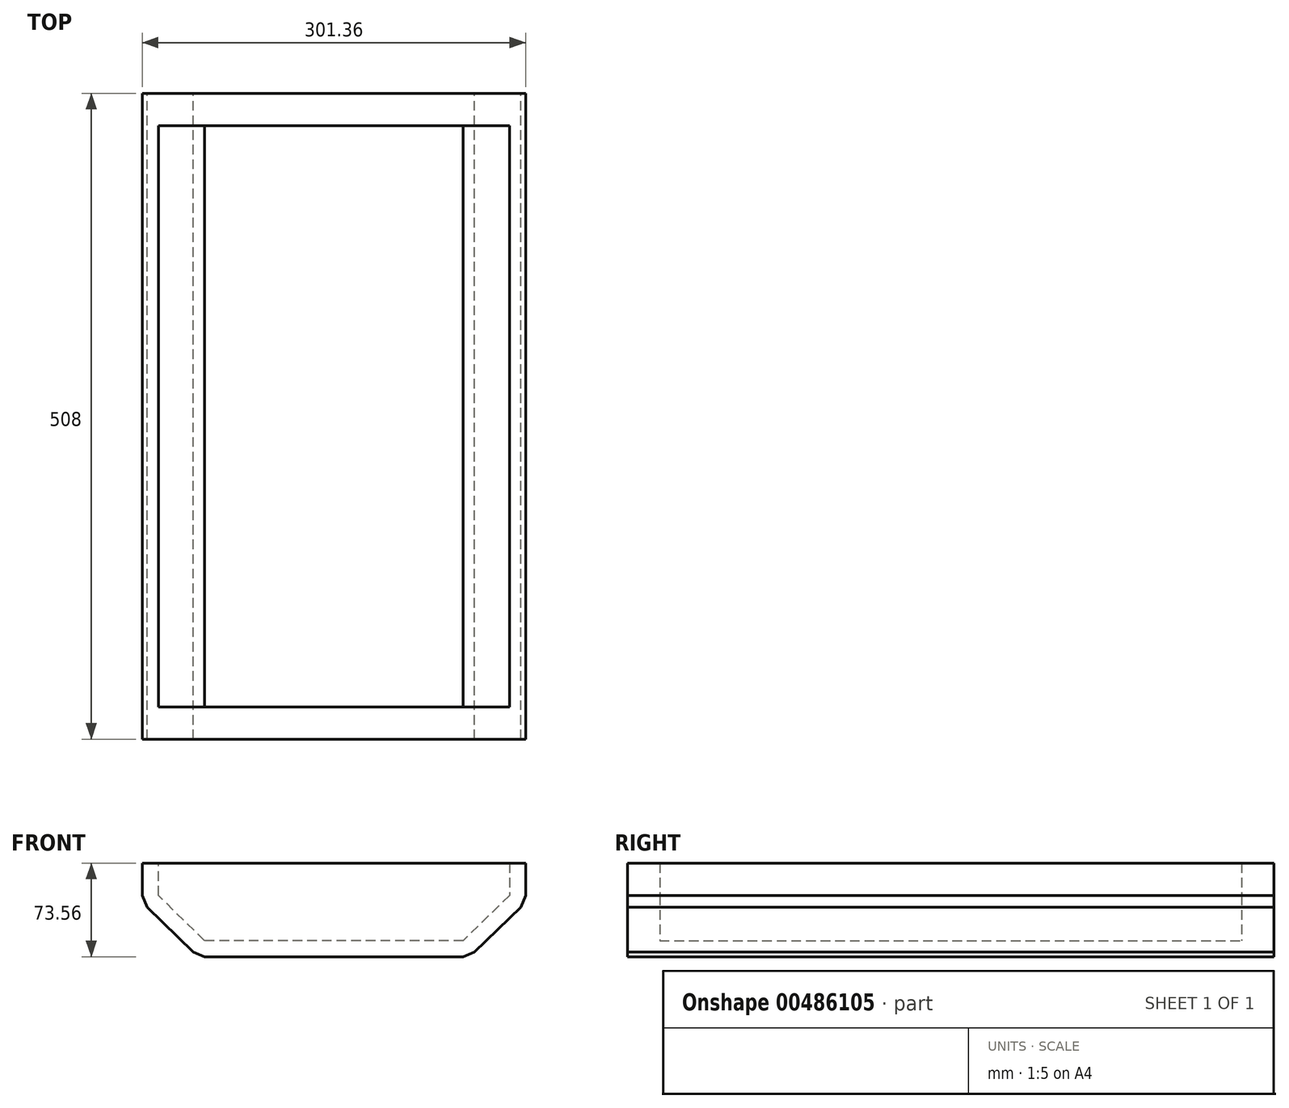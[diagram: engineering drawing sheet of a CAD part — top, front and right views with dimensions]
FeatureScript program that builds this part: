
annotation { "Feature Type Name" : "Feature", "Feature Type Description" : "" }
export const myFeature = defineFeature(function(context is Context, id is Id, definition is map)
    precondition{}
    {
        {
            var Q0;
            Q0=qCreatedBy(makeId("Front.planeOp"),FACE);
            var sketch = newSketch(context, id + "F0", { "sketchPlane" : qUnion([Q0])});
            skLineSegment(sketch, "E0", {"start": v(96.03, 17.25) * mm, "end": v(96.03, -8.15) * mm});
            skLineSegment(sketch, "E1", {"start": v(96.03, -8.15) * mm, "end": v(59.65, -43.61) * mm});
            skLineSegment(sketch, "E2", {"start": v(59.65, -43.61) * mm, "end": v(-143.55, -43.61) * mm});
            skLineSegment(sketch, "E3", {"start": v(-143.55, -43.61) * mm, "end": v(-179.93, -8.15) * mm});
            skLineSegment(sketch, "E4", {"start": v(-179.93, -8.15) * mm, "end": v(-179.93, 17.25) * mm});
            skLineSegment(sketch, "E5", {"start": v(-179.93, -8.15) * mm, "end": v(-188.8, -17.25) * mm});
            skLineSegment(sketch, "E6", {"start": v(96.03, -8.15) * mm, "end": v(104.9, -17.25) * mm});
            skLineSegment(sketch, "E7", {"start": v(-179.93, 17.25) * mm, "end": v(-192.63, 17.25) * mm});
            skLineSegment(sketch, "E8", {"start": v(96.03, 17.25) * mm, "end": v(108.73, 17.25) * mm});
            skLineSegment(sketch, "E9", {"start": v(59.65, -43.61) * mm, "end": v(68.52, -52.7) * mm});
            skLineSegment(sketch, "E10", {"start": v(-143.55, -43.61) * mm, "end": v(-152.41, -52.7) * mm});
            skLineSegment(sketch, "E11", {"start": v(-188.8, -17.25) * mm, "end": v(-152.41, -52.7) * mm});
            skLineSegment(sketch, "E12", {"start": v(-143.55, -43.61) * mm, "end": v(-143.55, -56.31) * mm});
            skLineSegment(sketch, "E13", {"start": v(59.65, -43.61) * mm, "end": v(59.65, -56.31) * mm});
            skLineSegment(sketch, "E14", {"start": v(59.65, -56.31) * mm, "end": v(-143.55, -56.31) * mm});
            skLineSegment(sketch, "E15", {"start": v(104.9, -17.25) * mm, "end": v(68.52, -52.7) * mm});
            skLineSegment(sketch, "E16", {"start": v(-179.93, -8.15) * mm, "end": v(-192.63, -8.15) * mm});
            skLineSegment(sketch, "E17", {"start": v(-192.63, -8.15) * mm, "end": v(-192.63, 17.25) * mm});
            skLineSegment(sketch, "E18", {"start": v(96.03, -8.15) * mm, "end": v(108.73, -8.15) * mm});
            skLineSegment(sketch, "E19", {"start": v(108.73, -8.15) * mm, "end": v(108.73, 17.25) * mm});
            skLineSegment(sketch, "E20", {"start": v(108.73, -8.15) * mm, "end": v(104.9, -17.25) * mm});
            skLineSegment(sketch, "E21", {"start": v(68.52, -52.7) * mm, "end": v(59.65, -56.31) * mm});
            skLineSegment(sketch, "E22", {"start": v(-152.41, -52.7) * mm, "end": v(-143.55, -56.31) * mm});
            skLineSegment(sketch, "E23", {"start": v(-192.63, -8.15) * mm, "end": v(-188.8, -17.25) * mm});
            skSolve(sketch);
        }
        {
            var Q0;
            Q0 = qSketchRegion(id + "F0", true);
            extrude(context, id + "F1", {"entities" : qUnion([Q0]), "depth" : 508 * mm});
        }
        {
            var Q0;
            Q0=qCreatedBy(makeId("Front.planeOp"),FACE);
            var sketch = newSketch(context, id + "F2", { "sketchPlane" : qUnion([Q0])});
            skLineSegment(sketch, "E24", {"start": v(-179.93, 17.25) * mm, "end": v(96.03, 17.25) * mm});
            skLineSegment(sketch, "E25", {"start": v(96.03, 17.25) * mm, "end": v(96.03, -8.15) * mm});
            skLineSegment(sketch, "E26", {"start": v(96.03, -8.15) * mm, "end": v(59.65, -43.61) * mm});
            skLineSegment(sketch, "E27", {"start": v(59.65, -43.61) * mm, "end": v(-143.55, -43.61) * mm});
            skLineSegment(sketch, "E28", {"start": v(-143.55, -43.61) * mm, "end": v(-179.93, -8.15) * mm});
            skLineSegment(sketch, "E29", {"start": v(-179.93, -8.15) * mm, "end": v(-179.93, 17.25) * mm});
            skSolve(sketch);
        }
        {
            var Q0;
            Q0=makeQuery(id+"F2.imprint","IMPRINT",FACE,{"disambiguationData":[TD([[makeQuery(id+"F2.imprint","IMPRINT",EDGE,{"derivedFrom":sQuery(id+"F2.wireOp",EDGE,"E24")}),-1.0]])]});
            extrude(context, id + "F3", {"entities" : qUnion([Q0]), "operationType" : NewBodyOperationType.ADD, "depth" : 25.4 * mm});
        }
        {
            var Q0;
            Q0=makeQuery(id+"F1.opExtrude","CAP_FACE",FACE,{"disambiguationData":[OSD([sQuery(id+"F0.wireOp",EDGE,"E0"),sQuery(id+"F0.wireOp",EDGE,"E1"),sQuery(id+"F0.wireOp",EDGE,"E2"),sQuery(id+"F0.wireOp",EDGE,"E3"),sQuery(id+"F0.wireOp",EDGE,"E4"),sQuery(id+"F0.wireOp",EDGE,"E7"),sQuery(id+"F0.wireOp",EDGE,"E8"),sQuery(id+"F0.wireOp",EDGE,"E11"),sQuery(id+"F0.wireOp",EDGE,"E14"),sQuery(id+"F0.wireOp",EDGE,"E15"),sQuery(id+"F0.wireOp",EDGE,"E17"),sQuery(id+"F0.wireOp",EDGE,"E19"),sQuery(id+"F0.wireOp",EDGE,"E20"),sQuery(id+"F0.wireOp",EDGE,"E21"),sQuery(id+"F0.wireOp",EDGE,"E22"),sQuery(id+"F0.wireOp",EDGE,"E23")])],"isStart":false});
            var sketch = newSketch(context, id + "F4", { "sketchPlane" : qUnion([Q0])});
            skLineSegment(sketch, "E30", {"start": v(-179.93, 17.25) * mm, "end": v(96.03, 17.25) * mm});
            skLineSegment(sketch, "E31", {"start": v(96.03, 17.25) * mm, "end": v(96.03, -8.15) * mm});
            skLineSegment(sketch, "E32", {"start": v(96.03, -8.15) * mm, "end": v(59.65, -43.61) * mm});
            skLineSegment(sketch, "E33", {"start": v(59.65, -43.61) * mm, "end": v(-143.55, -43.61) * mm});
            skLineSegment(sketch, "E34", {"start": v(-143.55, -43.61) * mm, "end": v(-179.93, -8.15) * mm});
            skLineSegment(sketch, "E35", {"start": v(-179.93, -8.15) * mm, "end": v(-179.93, 17.25) * mm});
            skSolve(sketch);
        }
        {
            var Q0;
            Q0=makeQuery(id+"F4.imprint","IMPRINT",FACE,{"disambiguationData":[TD([[makeQuery(id+"F4.imprint","IMPRINT",EDGE,{"derivedFrom":sQuery(id+"F4.wireOp",EDGE,"E30")}),-1.0]])]});
            extrude(context, id + "F5", {"entities" : qUnion([Q0]), "operationType" : NewBodyOperationType.ADD, "oppositeDirection" : true, "depth" : 25.4 * mm});
        }
    });
